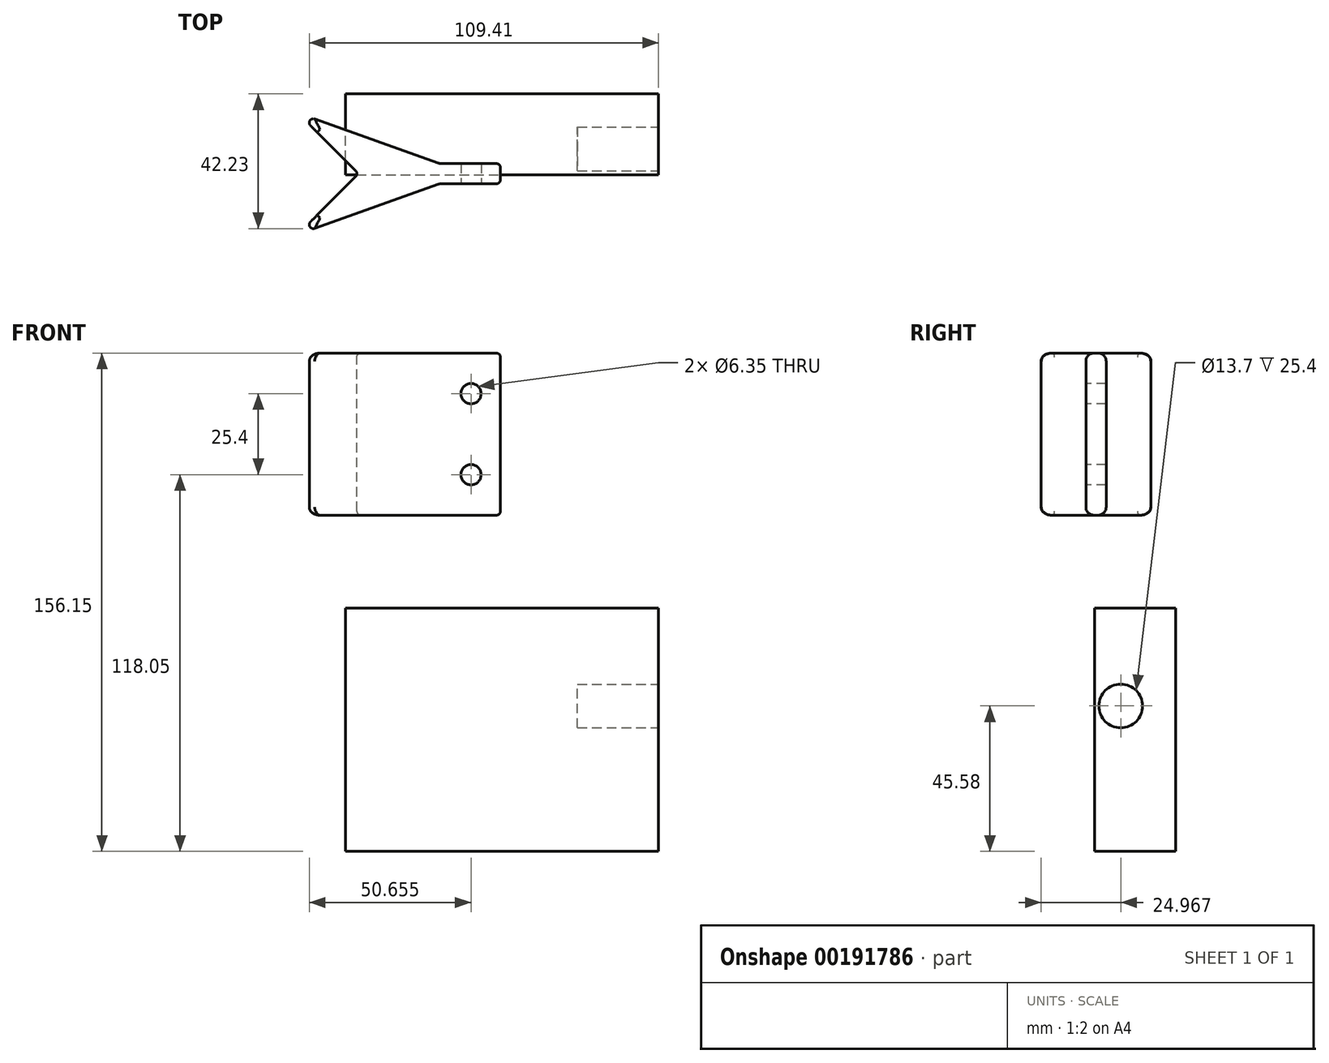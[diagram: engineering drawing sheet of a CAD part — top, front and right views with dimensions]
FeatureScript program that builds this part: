
annotation { "Feature Type Name" : "Feature", "Feature Type Description" : "" }
export const myFeature = defineFeature(function(context is Context, id is Id, definition is map)
    precondition{}
    {
        {
            var Q0;
            Q0=qCreatedBy(makeId("Top.planeOp"),FACE);
            var sketch = newSketch(context, id + "F0", { "sketchPlane" : qUnion([Q0])});
            skLineSegment(sketch, "E0.right", {"start": v(-14.85, -21.83) * mm, "end": v(-14.85, -28.18) * mm});
            skLineSegment(sketch, "E1", {"start": v(-59.3, -5.95) * mm, "end": v(-40.25, -25) * mm});
            skLineSegment(sketch, "E2", {"start": v(-40.25, -25) * mm, "end": v(-59.3, -44.05) * mm});
            skLineSegment(sketch, "E3.bottom", {"start": v(-14.85, -21.83) * mm, "end": v(4.2, -21.83) * mm});
            skLineSegment(sketch, "E3.top", {"start": v(-14.85, -28.18) * mm, "end": v(4.2, -28.18) * mm});
            skLineSegment(sketch, "E3.right", {"start": v(4.2, -21.83) * mm, "end": v(4.2, -28.18) * mm});
            skLineSegment(sketch, "E4", {"start": v(-59.3, -5.95) * mm, "end": v(-14.85, -21.83) * mm});
            skLineSegment(sketch, "E5", {"start": v(-59.3, -44.05) * mm, "end": v(-14.85, -28.18) * mm});
            skSolve(sketch);
        }
        {
            var Q0;
            Q0=makeQuery(id+"F0.imprint","IMPRINT",FACE,{"disambiguationData":[TD([[makeQuery(id+"F0.imprint","IMPRINT",EDGE,{"derivedFrom":sQuery(id+"F0.wireOp",EDGE,"E0.bottom")}),-1.0]])]});
            var Q1;
            Q1=makeQuery(id+"F0.imprint","IMPRINT",FACE,{"disambiguationData":[TD([[makeQuery(id+"F0.imprint","IMPRINT",EDGE,{"derivedFrom":sQuery(id+"F0.wireOp",EDGE,"E3.bottom")}),-1.0]])]});
            var Q2;
            Q2=makeQuery(id+"F0.imprint","IMPRINT",FACE,{"disambiguationData":[TD([[makeQuery(id+"F0.imprint","IMPRINT",EDGE,{"derivedFrom":sQuery(id+"F0.wireOp",EDGE,"E1")}),1.0]])]});
            extrude(context, id + "F1", {"entities" : qUnion([Q0, Q1, Q2]), "depth" : 50.8 * mm});
        }
        {
            var Q0;
            Q0=makeQuery(id+"F1.opExtrude","CAP_EDGE",EDGE,{"disambiguationData":[OSD([sQuery(id+"F0.wireOp",EDGE,"E0.bottom")])],"isStart":true});
            var Q1;
            Q1=makeQuery(id+"F1.opExtrude","CAP_EDGE",EDGE,{"disambiguationData":[OSD([sQuery(id+"F0.wireOp",EDGE,"E0.bottom")])],"isStart":false});
            var Q2;
            Q2=makeQuery(id+"F1.opExtrude","SWEPT_EDGE",EDGE,{"disambiguationData":[OSD([sQuery(id+"F0.wireOp",EDGE,"E0.bottom"),sQuery(id+"F0.wireOp",EDGE,"E1")])]});
            var Q3;
            Q3=makeQuery(id+"F1.opExtrude","CAP_EDGE",EDGE,{"disambiguationData":[OSD([sQuery(id+"F0.wireOp",EDGE,"E0.top")])],"isStart":false});
            var Q4;
            Q4=makeQuery(id+"F1.opExtrude","SWEPT_EDGE",EDGE,{"disambiguationData":[OSD([sQuery(id+"F0.wireOp",EDGE,"E0.top"),sQuery(id+"F0.wireOp",EDGE,"E2")])]});
            var Q5;
            Q5=makeQuery(id+"F1.opExtrude","CAP_EDGE",EDGE,{"disambiguationData":[OSD([sQuery(id+"F0.wireOp",EDGE,"E0.top")])],"isStart":true});
            var Q6;
            Q6=makeQuery(id+"F1.opExtrude","CAP_EDGE",EDGE,{"disambiguationData":[OSD([sQuery(id+"F0.wireOp",EDGE,"E2")])],"isStart":true});
            var Q7;
            Q7=makeQuery(id+"F1.opExtrude","CAP_EDGE",EDGE,{"disambiguationData":[OSD([sQuery(id+"F0.wireOp",EDGE,"E1")])],"isStart":true});
            var Q8;
            Q8=makeQuery(id+"F1.opExtrude","CAP_EDGE",EDGE,{"disambiguationData":[OSD([sQuery(id+"F0.wireOp",EDGE,"E2")])],"isStart":false});
            var Q9;
            Q9=makeQuery(id+"F1.opExtrude","CAP_EDGE",EDGE,{"disambiguationData":[OSD([sQuery(id+"F0.wireOp",EDGE,"E1")])],"isStart":false});
            fillet(context, id + "F2", {"entities" : qUnion([Q0, Q1, Q2, Q3, Q4, Q5, Q6, Q7, Q8, Q9]), "radius" : 1.27 * mm, "tangentPropagation" : true, "allowEdgeOverflow" : false});
        }
        {
            var Q0;
            Q0=makeQuery(id+"F1.opExtrude","SWEPT_FACE",FACE,{"disambiguationData":[OSD([sQuery(id+"F0.wireOp",EDGE,"E3.top")])]});
            var sketch = newSketch(context, id + "F3", { "sketchPlane" : qUnion([Q0])});
            skCircle(sketch, "E6", {"center": v(-5.02, 38.1) * mm, "radius": 3.18 * mm});
            skCircle(sketch, "E7", {"center": v(-5.02, 12.7) * mm, "radius": 3.18 * mm});
            skSolve(sketch);
        }
        {
            var Q0;
            Q0=qSketchRegion(id+"F3",true);
            extrude(context, id + "F4", {"entities" : qUnion([Q0]), "operationType" : NewBodyOperationType.REMOVE, "oppositeDirection" : true, "depth" : 25.4 * mm});
        }
        {
            var Q0;
            Q0=makeQuery(id+"F1.opExtrude","CAP_EDGE",EDGE,{"disambiguationData":[OSD([sQuery(id+"F0.wireOp",EDGE,"E4")])],"isStart":true});
            var Q1;
            Q1=makeQuery(id+"F1.opExtrude","CAP_EDGE",EDGE,{"disambiguationData":[OSD([sQuery(id+"F0.wireOp",EDGE,"E5")])],"isStart":true});
            var Q2;
            Q2=makeQuery(id+"F1.opExtrude","CAP_EDGE",EDGE,{"disambiguationData":[OSD([sQuery(id+"F0.wireOp",EDGE,"E3.top")])],"isStart":true});
            var Q3;
            Q3=makeQuery(id+"F1.opExtrude","CAP_EDGE",EDGE,{"disambiguationData":[OSD([sQuery(id+"F0.wireOp",EDGE,"E5")])],"isStart":false});
            var Q4;
            Q4=makeQuery(id+"F1.opExtrude","CAP_EDGE",EDGE,{"disambiguationData":[OSD([sQuery(id+"F0.wireOp",EDGE,"E3.top")])],"isStart":false});
            var Q5;
            Q5=makeQuery(id+"F1.opExtrude","CAP_EDGE",EDGE,{"disambiguationData":[OSD([sQuery(id+"F0.wireOp",EDGE,"E4")])],"isStart":false});
            var Q6;
            Q6=makeQuery(id+"F1.opExtrude","CAP_EDGE",EDGE,{"disambiguationData":[OSD([sQuery(id+"F0.wireOp",EDGE,"E3.bottom")])],"isStart":false});
            var Q7;
            Q7=makeQuery(id+"F1.opExtrude","CAP_EDGE",EDGE,{"disambiguationData":[OSD([sQuery(id+"F0.wireOp",EDGE,"E3.bottom")])],"isStart":true});
            var Q8;
            Q8=makeQuery(id+"F1.opExtrude","SWEPT_EDGE",EDGE,{"disambiguationData":[OSD([sQuery(id+"F0.wireOp",EDGE,"E3.bottom"),sQuery(id+"F0.wireOp",EDGE,"E0.right"),sQuery(id+"F0.wireOp",EDGE,"E4")])]});
            var Q9;
            Q9=makeQuery(id+"F1.opExtrude","SWEPT_EDGE",EDGE,{"disambiguationData":[OSD([sQuery(id+"F0.wireOp",EDGE,"E3.top"),sQuery(id+"F0.wireOp",EDGE,"E0.right"),sQuery(id+"F0.wireOp",EDGE,"E5")])]});
            fillet(context, id + "F5", {"entities" : qUnion([Q0, Q1, Q2, Q3, Q4, Q5, Q6, Q7, Q8, Q9]), "radius" : 2.54 * mm, "tangentPropagation" : true, "allowEdgeOverflow" : false});
        }
        {
            var Q0;
            Q0=makeQuery(id+"F1.opExtrude","CAP_EDGE",EDGE,{"disambiguationData":[OSD([sQuery(id+"F0.wireOp",EDGE,"E3.top")])],"isStart":true});
            var Q1;
            Q1=makeQuery(id+"F1.opExtrude","SWEPT_EDGE",EDGE,{"disambiguationData":[OSD([sQuery(id+"F0.wireOp",EDGE,"E3.top"),sQuery(id+"F0.wireOp",EDGE,"E3.right")])]});
            var Q2;
            Q2=makeQuery(id+"F1.opExtrude","CAP_EDGE",EDGE,{"disambiguationData":[OSD([sQuery(id+"F0.wireOp",EDGE,"E3.top")])],"isStart":false});
            var Q3;
            Q3=makeQuery(id+"F1.opExtrude","CAP_EDGE",EDGE,{"disambiguationData":[OSD([sQuery(id+"F0.wireOp",EDGE,"E3.bottom")])],"isStart":true});
            var Q4;
            Q4=makeQuery(id+"F1.opExtrude","CAP_EDGE",EDGE,{"disambiguationData":[OSD([sQuery(id+"F0.wireOp",EDGE,"E3.bottom")])],"isStart":false});
            var Q5;
            Q5=makeQuery(id+"F1.opExtrude","SWEPT_EDGE",EDGE,{"disambiguationData":[OSD([sQuery(id+"F0.wireOp",EDGE,"E3.bottom"),sQuery(id+"F0.wireOp",EDGE,"E3.right")])]});
            var Q6;
            Q6=makeQuery(id+"F1.opExtrude","CAP_EDGE",EDGE,{"disambiguationData":[OSD([sQuery(id+"F0.wireOp",EDGE,"E3.right")])],"isStart":false});
            var Q7;
            Q7=makeQuery(id+"F1.opExtrude","CAP_EDGE",EDGE,{"disambiguationData":[OSD([sQuery(id+"F0.wireOp",EDGE,"E3.right")])],"isStart":true});
            fillet(context, id + "F6", {"entities" : qUnion([Q0, Q1, Q2, Q3, Q4, Q5, Q6, Q7]), "radius" : 1.27 * mm, "tangentPropagation" : true, "allowEdgeOverflow" : false});
        }
        {
            var Q0;
            Q0=qCreatedBy(makeId("Front.planeOp"),FACE);
            var sketch = newSketch(context, id + "F7", { "sketchPlane" : qUnion([Q0])});
            skLineSegment(sketch, "E8.bottom", {"start": v(-44.4, -29.13) * mm, "end": v(53.73, -29.13) * mm});
            skLineSegment(sketch, "E8.top", {"start": v(-44.4, -105.35) * mm, "end": v(53.73, -105.35) * mm});
            skLineSegment(sketch, "E8.left", {"start": v(-44.4, -29.13) * mm, "end": v(-44.4, -105.35) * mm});
            skLineSegment(sketch, "E8.right", {"start": v(53.73, -29.13) * mm, "end": v(53.73, -105.35) * mm});
            skSolve(sketch);
        }
        {
            var Q0;
            Q0 = qSketchRegion(id + "F7", true);
            extrude(context, id + "F8", {"entities" : qUnion([Q0]), "depth" : 25.4 * mm, "offsetDistance" : 25.4 * mm});
        }
        {
            var Q0;
            Q0=makeQuery(id+"F8.opExtrude","SWEPT_FACE",FACE,{"disambiguationData":[OSD([sQuery(id+"F7.wireOp",EDGE,"E8.right")])]});
            var sketch = newSketch(context, id + "F9", { "sketchPlane" : qUnion([Q0])});
            skCircle(sketch, "E9", {"center": v(-17.26, -59.77) * mm, "radius": 6.85 * mm});
            skSolve(sketch);
        }
        {
            var Q0;
            Q0 = qSketchRegion(id + "F9", true);
            extrude(context, id + "F10", {"entities" : qUnion([Q0]), "operationType" : NewBodyOperationType.REMOVE, "oppositeDirection" : true, "depth" : 25.4 * mm, "offsetDistance" : 25.4 * mm});
        }
    });
